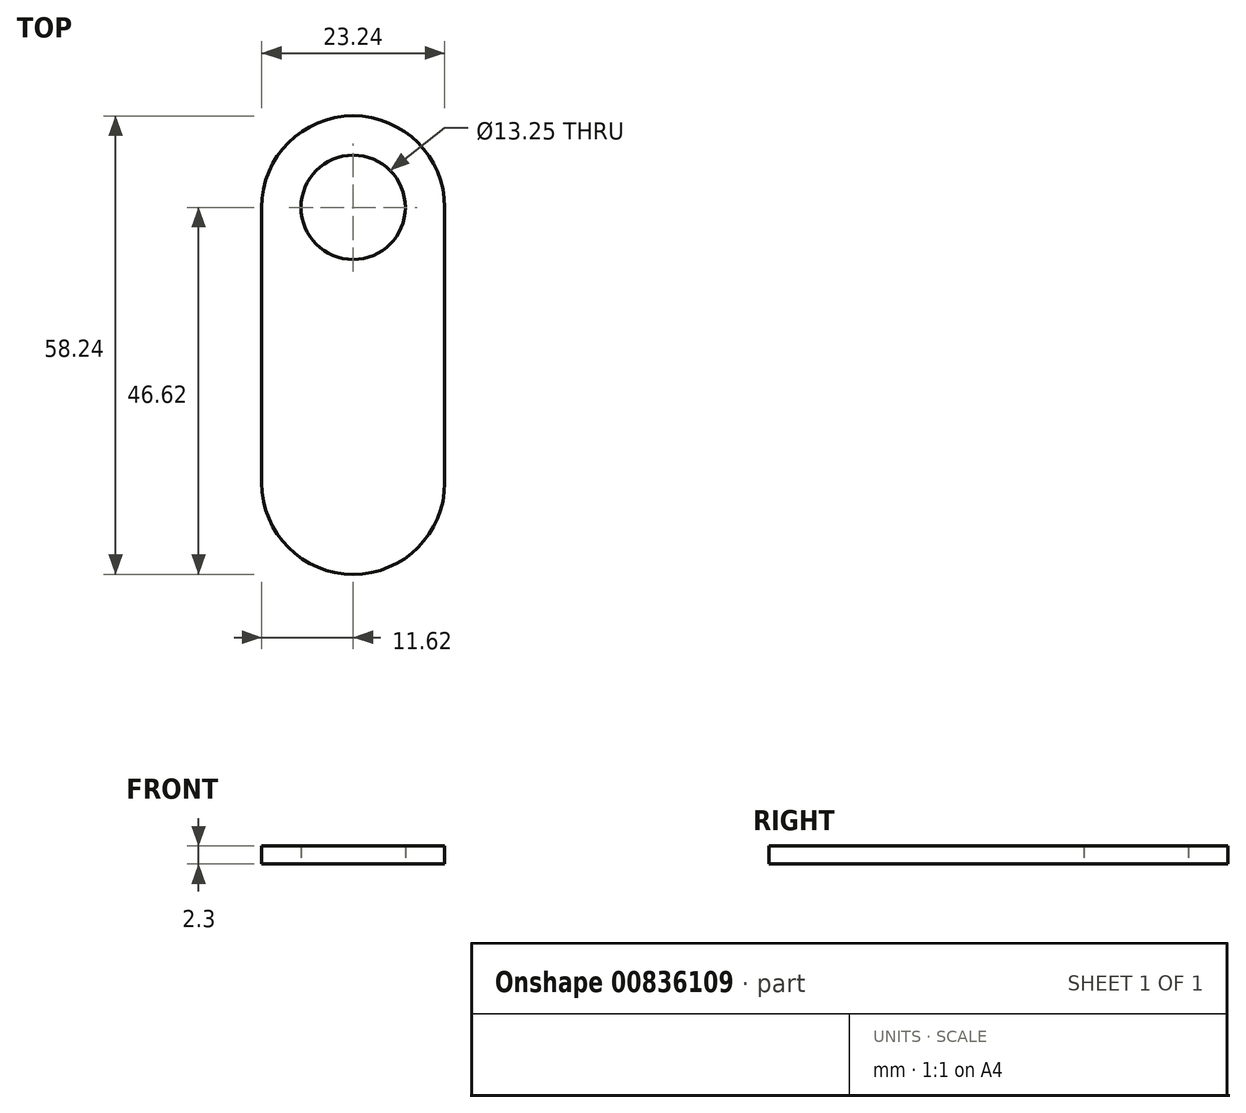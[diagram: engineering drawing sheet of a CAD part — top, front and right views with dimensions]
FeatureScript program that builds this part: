
annotation { "Feature Type Name" : "Feature", "Feature Type Description" : "" }
export const myFeature = defineFeature(function(context is Context, id is Id, definition is map)
    precondition{}
    {
        {
            var Q0;
            Q0=qCreatedBy(makeId("Top.planeOp"),FACE);
            var sketch = newSketch(context, id + "F0", { "sketchPlane" : qUnion([Q0])});
            skCircle(sketch, "E0", {"center": v(0, 0) * mm, "radius": 11.62 * mm});
            skLineSegment(sketch, "E1", {"start": v(-11.62, 0) * mm, "end": v(-11.62, -35) * mm});
            skLineSegment(sketch, "E2", {"start": v(11.62, -35) * mm, "end": v(11.62, 0) * mm});
            skCircle(sketch, "E3", {"center": v(0, -35) * mm, "radius": 11.62 * mm});
            skCircle(sketch, "E4", {"center": v(0, 0) * mm, "radius": 6.62 * mm});
            skSolve(sketch);
        }
        {
            var Q0;
            {var subQ0=sQuery(id+"F0.wireOp",EDGE,"E3");var subQ1=makeQuery(id+"F0.imprint","INTERSECT",VERTEX,{"derivedFrom":[sQuery(id+"F0.wireOp",EDGE,"E1"),subQ0]});Q0=makeQuery(id+"F0.imprint","IMPRINT",FACE,{"disambiguationData":[TD([[makeQuery(id+"F0.imprint","IMPRINT",EDGE,{"disambiguationData":[TD([[subQ1,1.0]])],"derivedFrom":subQ0}),1.0]])]});}
            var Q1;
            {var subQ0=sQuery(id+"F0.wireOp",EDGE,"E1");Q1=makeQuery(id+"F0.imprint","IMPRINT",FACE,{"disambiguationData":[TD([[makeQuery(id+"F0.imprint","IMPRINT",EDGE,{"derivedFrom":subQ0}),1.0]])]});}
            var Q2;
            Q2=makeQuery(id+"F0.imprint","IMPRINT",FACE,{"disambiguationData":[TD([[makeQuery(id+"F0.imprint","IMPRINT",EDGE,{"derivedFrom":sQuery(id+"F0.wireOp",EDGE,"E4")}),-1.0]])]});
            extrude(context, id + "F1", {"entities" : qUnion([Q0, Q1, Q2]), "depth" : 2.3 * mm, "offsetDistance" : 25 * mm});
        }
    });
